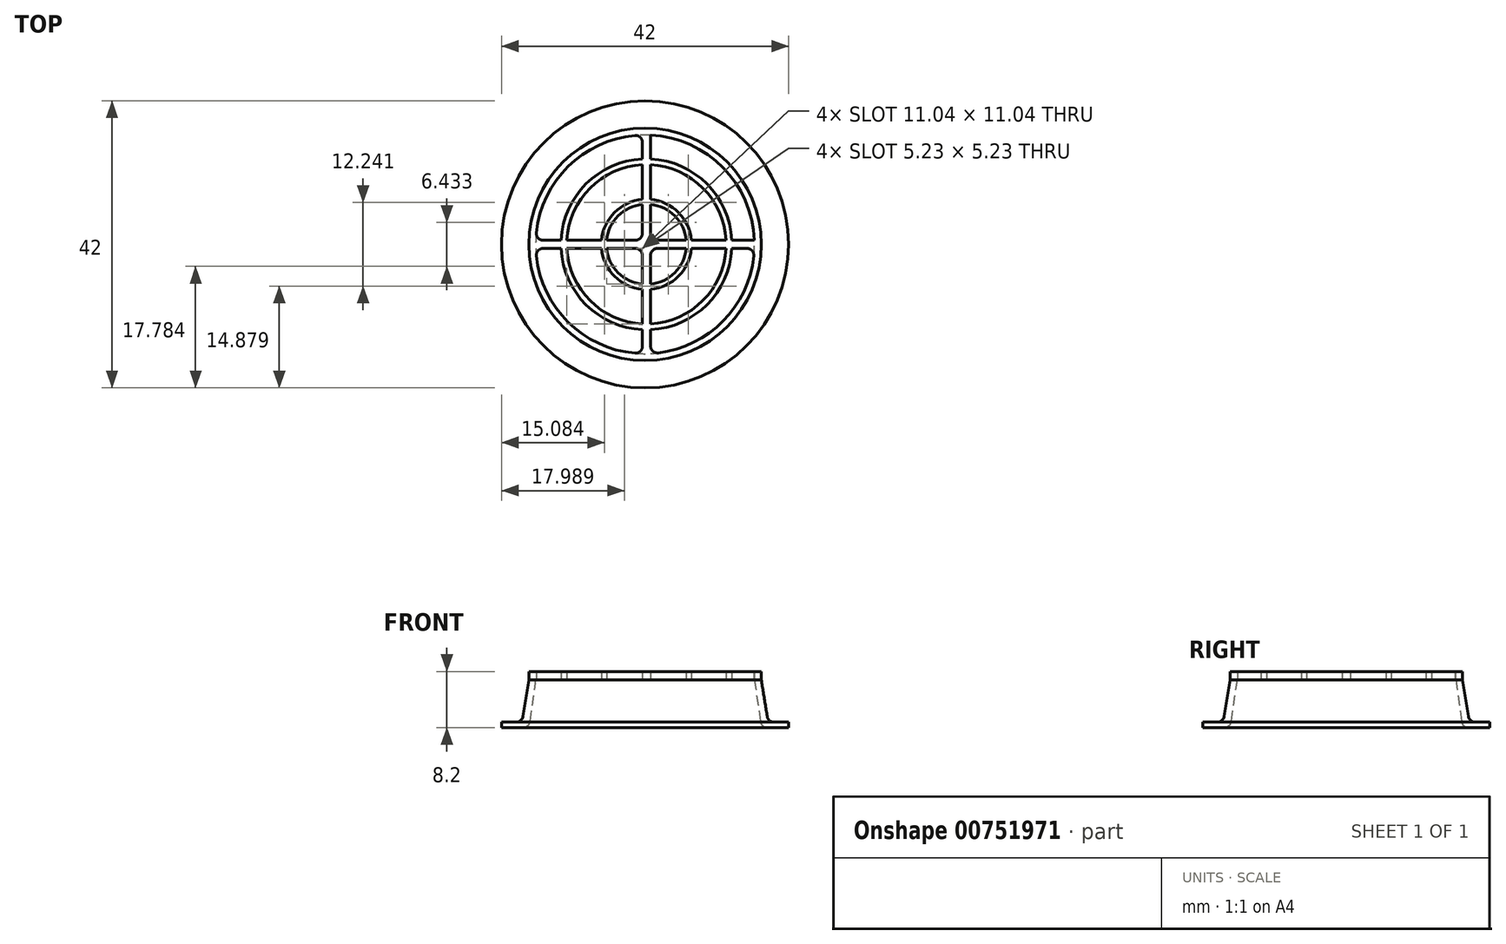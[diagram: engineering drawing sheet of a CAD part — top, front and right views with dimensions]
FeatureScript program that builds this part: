
annotation { "Feature Type Name" : "Feature", "Feature Type Description" : "" }
export const myFeature = defineFeature(function(context is Context, id is Id, definition is map)
    precondition{}
    {
        {
            var Q0;
            Q0=qCreatedBy(makeId("Front.planeOp"),FACE);
            var sketch = newSketch(context, id + "F0", { "sketchPlane" : qUnion([Q0])});
            skLineSegment(sketch, "E0", {"start": v(0, 16.66) * mm, "end": v(0, -15.75) * mm, "construction": true});
            skLineSegment(sketch, "E1", {"start": v(8.08, 0) * mm, "end": v(-29.3, 0) * mm, "construction": true});
            skLineSegment(sketch, "E2", {"start": v(1.58, 0) * mm, "end": v(-1.66, 0) * mm, "construction": true});
            skLineSegment(sketch, "E3", {"start": v(-1, 1.45) * mm, "end": v(-1, -7.95) * mm, "construction": true});
            skLineSegment(sketch, "E4", {"start": v(-5, -6.2) * mm, "end": v(-5, -8.06) * mm, "construction": true});
            skLineSegment(sketch, "E5", {"start": v(-5, -7) * mm, "end": v(-1.87, -7) * mm});
            skLineSegment(sketch, "E6", {"start": v(-0.88, -6.14) * mm, "end": v(0, 0) * mm});
            skLineSegment(sketch, "E7", {"start": v(0, 0) * mm, "end": v(-1, 0) * mm});
            skLineSegment(sketch, "E8", {"start": v(-1, 0) * mm, "end": v(-1.86, -5.36) * mm});
            skLineSegment(sketch, "E9", {"start": v(-2.85, -6.2) * mm, "end": v(-5, -6.2) * mm});
            skLineSegment(sketch, "E10", {"start": v(-5, -6.2) * mm, "end": v(-5, -7) * mm});
            skPoint(sketch, "E11.visualSharp", {"position": v(-2, -6.2) * mm});
            skArc(sketch, "E11.filletArc", {"start": v(-2.85, -6.2) * mm, "mid": v(-2.2, -5.96) * mm, "end": v(-1.86, -5.36) * mm});
            skPoint(sketch, "E12.visualSharp", {"position": v(-1, -7) * mm});
            skArc(sketch, "E12.filletArc", {"start": v(-1.87, -7) * mm, "mid": v(-1.21, -6.76) * mm, "end": v(-0.88, -6.14) * mm});
            skLineSegment(sketch, "E13", {"start": v(16, 0.36) * mm, "end": v(16, -7.36) * mm, "construction": true});
            skSolve(sketch);
        }
        {
            var Q0;
            Q0 = qSketchRegion(id + "F0", true);
            var Q1;
            Q1=sQuery(id+"F0.wireOp",EDGE,"E13");
            revolve(context, id + "F1", {"surfaceOperationType" : NewSurfaceOperationType.NEW, "entities" : qUnion([Q0]), "axis" : qUnion([Q1]), "revolveType" : RevolveType.FULL});
        }
        {
            var Q0;
            Q0=qCreatedBy(makeId("Top.planeOp"),FACE);
            var sketch = newSketch(context, id + "F2", { "sketchPlane" : qUnion([Q0])});
            skLineSegment(sketch, "E14", {"start": v(0, 0) * mm, "end": v(32.4, 0) * mm, "construction": true});
            skLineSegment(sketch, "E15", {"start": v(0.01, 0.6) * mm, "end": v(3.72, 0.6) * mm});
            skLineSegment(sketch, "E16.MirrorCS", {"start": v(0.01, -0.6) * mm, "end": v(3.72, -0.6) * mm});
            skLineSegment(sketch, "E17", {"start": v(16.2, 0) * mm, "end": v(16.2, 17) * mm, "construction": true});
            skLineSegment(sketch, "E18", {"start": v(15.6, 16) * mm, "end": v(15.6, 12.48) * mm});
            skLineSegment(sketch, "E19.MirrorCS", {"start": v(16.8, 15.98) * mm, "end": v(16.8, 12.48) * mm});
            skArc(sketch, "E20", {"start": v(15.6, 5.83) * mm, "mid": v(12.06, 4.15) * mm, "end": v(10.37, 0.6) * mm});
            skArc(sketch, "E21", {"start": v(15.6, 11.64) * mm, "mid": v(7.96, 8.24) * mm, "end": v(4.56, 0.6) * mm});
            skArc(sketch, "E22", {"start": v(15.6, 6.58) * mm, "mid": v(11.53, 4.67) * mm, "end": v(9.63, 0.6) * mm});
            skArc(sketch, "E23", {"start": v(15.6, 12.48) * mm, "mid": v(7.37, 8.84) * mm, "end": v(3.72, 0.6) * mm});
            skLineSegment(sketch, "E24.trimOffspring", {"start": v(16.8, 11.64) * mm, "end": v(16.8, 6.58) * mm});
            skLineSegment(sketch, "E25.trimOffspring", {"start": v(15.6, 11.64) * mm, "end": v(15.6, 6.58) * mm});
            skLineSegment(sketch, "E26.trimOffspring", {"start": v(15.6, 5.83) * mm, "end": v(15.6, 1.6) * mm});
            skLineSegment(sketch, "E27.trimOffspring", {"start": v(16.8, 5.83) * mm, "end": v(16.8, 1.6) * mm});
            skArc(sketch, "E28.trimOffspring", {"start": v(27.85, 0.6) * mm, "mid": v(24.45, 8.24) * mm, "end": v(16.8, 11.64) * mm});
            skLineSegment(sketch, "E29.trimOffspring", {"start": v(28.69, -0.6) * mm, "end": v(31.99, -0.6) * mm});
            skArc(sketch, "E30.trimOffspring", {"start": v(28.69, 0.6) * mm, "mid": v(25.04, 8.84) * mm, "end": v(16.8, 12.48) * mm});
            skLineSegment(sketch, "E31.trimOffspring", {"start": v(28.69, 0.6) * mm, "end": v(31.99, 0.6) * mm});
            skArc(sketch, "E32.trimOffspring", {"start": v(3.72, -0.6) * mm, "mid": v(7.37, -8.84) * mm, "end": v(15.6, -12.48) * mm});
            skArc(sketch, "E33.trimOffspring", {"start": v(4.56, -0.6) * mm, "mid": v(7.96, -8.24) * mm, "end": v(15.6, -11.64) * mm});
            skLineSegment(sketch, "E34.trimOffspring", {"start": v(4.56, 0.6) * mm, "end": v(9.63, 0.6) * mm});
            skLineSegment(sketch, "E35.trimOffspring", {"start": v(4.56, -0.6) * mm, "end": v(9.63, -0.6) * mm});
            skArc(sketch, "E36.trimOffspring", {"start": v(9.63, -0.6) * mm, "mid": v(11.53, -4.67) * mm, "end": v(15.6, -6.58) * mm});
            skLineSegment(sketch, "E37.trimOffspring", {"start": v(10.37, 0.6) * mm, "end": v(14.6, 0.6) * mm});
            skArc(sketch, "E38.trimOffspring", {"start": v(10.37, -0.6) * mm, "mid": v(12.06, -4.15) * mm, "end": v(15.6, -5.83) * mm});
            skLineSegment(sketch, "E39.trimOffspring", {"start": v(10.37, -0.6) * mm, "end": v(14.6, -0.6) * mm});
            skArc(sketch, "E40.trimOffspring", {"start": v(22.04, 0.6) * mm, "mid": v(20.35, 4.15) * mm, "end": v(16.8, 5.83) * mm});
            skLineSegment(sketch, "E41.trimOffspring", {"start": v(22.78, -0.6) * mm, "end": v(27.85, -0.6) * mm});
            skArc(sketch, "E42.trimOffspring", {"start": v(22.78, 0.6) * mm, "mid": v(20.88, 4.67) * mm, "end": v(16.8, 6.58) * mm});
            skLineSegment(sketch, "E43.trimOffspring", {"start": v(15.6, -6.58) * mm, "end": v(15.6, -11.64) * mm});
            skArc(sketch, "E44.trimOffspring", {"start": v(16.8, -6.58) * mm, "mid": v(20.88, -4.67) * mm, "end": v(22.78, -0.6) * mm});
            skLineSegment(sketch, "E45.trimOffspring", {"start": v(16.8, -6.58) * mm, "end": v(16.8, -11.64) * mm});
            skArc(sketch, "E46.trimOffspring", {"start": v(16.8, -5.83) * mm, "mid": v(20.35, -4.15) * mm, "end": v(22.04, -0.6) * mm});
            skLineSegment(sketch, "E47.trimOffspring", {"start": v(15.6, -12.48) * mm, "end": v(15.6, -16) * mm});
            skArc(sketch, "E48.trimOffspring", {"start": v(16.8, -12.48) * mm, "mid": v(25.04, -8.84) * mm, "end": v(28.69, -0.6) * mm});
            skLineSegment(sketch, "E49.trimOffspring", {"start": v(16.8, -12.48) * mm, "end": v(16.8, -16) * mm});
            skArc(sketch, "E50.trimOffspring", {"start": v(16.8, -11.64) * mm, "mid": v(24.45, -8.24) * mm, "end": v(27.85, -0.6) * mm});
            skLineSegment(sketch, "E51", {"start": v(17.8, 0.6) * mm, "end": v(22.04, 0.6) * mm});
            skLineSegment(sketch, "E52", {"start": v(16.8, -1.6) * mm, "end": v(16.8, -5.83) * mm});
            skLineSegment(sketch, "E53", {"start": v(17.8, -0.6) * mm, "end": v(22.04, -0.6) * mm});
            skLineSegment(sketch, "E54.trimOffspring", {"start": v(15.6, -1.6) * mm, "end": v(15.6, -5.83) * mm});
            skPoint(sketch, "E55.visualSharp", {"position": v(15.6, 0.6) * mm});
            skArc(sketch, "E55.filletArc", {"start": v(14.6, 0.6) * mm, "mid": v(15.31, 0.9) * mm, "end": v(15.6, 1.6) * mm});
            skPoint(sketch, "E56.visualSharp", {"position": v(16.8, 0.6) * mm});
            skArc(sketch, "E56.filletArc", {"start": v(16.8, 1.6) * mm, "mid": v(17.1, 0.9) * mm, "end": v(17.8, 0.6) * mm});
            skPoint(sketch, "E57.visualSharp", {"position": v(16.8, -0.6) * mm});
            skArc(sketch, "E57.filletArc", {"start": v(17.8, -0.6) * mm, "mid": v(17.1, -0.9) * mm, "end": v(16.8, -1.6) * mm});
            skPoint(sketch, "E58.visualSharp", {"position": v(15.6, -0.6) * mm});
            skArc(sketch, "E58.filletArc", {"start": v(15.6, -1.6) * mm, "mid": v(15.31, -0.9) * mm, "end": v(14.6, -0.6) * mm});
            skLineSegment(sketch, "E59.trimOffspring", {"start": v(22.78, 0.6) * mm, "end": v(27.85, 0.6) * mm});
            skCircle(sketch, "E60.0", {"center": v(16, 0) * mm, "radius": 16 * mm});
            skPoint(sketch, "E61.orphan", {"position": v(16.8, 16) * mm});
            skSolve(sketch);
        }
        {
            var Q0;
            Q0=makeQuery(id+"F1.opRevolve","SWEPT_FACE",FACE,{"disambiguationData":[OSD([sQuery(id+"F0.wireOp",EDGE,"E7")])]});
            var Q1;
            {var subQ7=sQuery(id+"F2.wireOp",EDGE,"E15");Q1=makeQuery(id+"F2.imprint","IMPRINT",FACE,{"disambiguationData":[TD([[makeQuery(id+"F2.imprint","IMPRINT",EDGE,{"derivedFrom":subQ7}),-1.0]])]});}
            extrude(context, id + "F3", {"entities" : qUnion([Q0, Q1]), "operationType" : NewBodyOperationType.ADD, "depth" : 1.2 * mm, "offsetDistance" : 25 * mm});
        }
        {
            var Q0;
            Q0=makeQuery(id+"F3.opExtrude","SWEPT_EDGE",EDGE,{"disambiguationData":[OSD([sQuery(id+"F2.wireOp",EDGE,"E18"),sQuery(id+"F2.wireOp",EDGE,"E60.0")])]});
            var Q1;
            Q1=makeQuery(id+"F3.opExtrude","SWEPT_EDGE",EDGE,{"disambiguationData":[OSD([sQuery(id+"F2.wireOp",EDGE,"E19.MirrorCS"),sQuery(id+"F2.wireOp",EDGE,"E60.0")])]});
            var Q2;
            Q2=makeQuery(id+"F3.opExtrude","SWEPT_EDGE",EDGE,{"disambiguationData":[OSD([sQuery(id+"F2.wireOp",EDGE,"E29.trimOffspring"),sQuery(id+"F2.wireOp",EDGE,"E60.0")])]});
            var Q3;
            Q3=makeQuery(id+"F3.opExtrude","SWEPT_EDGE",EDGE,{"disambiguationData":[OSD([sQuery(id+"F2.wireOp",EDGE,"E31.trimOffspring"),sQuery(id+"F2.wireOp",EDGE,"E60.0")])]});
            var Q4;
            Q4=makeQuery(id+"F3.opExtrude","SWEPT_EDGE",EDGE,{"disambiguationData":[OSD([sQuery(id+"F2.wireOp",EDGE,"E47.trimOffspring"),sQuery(id+"F2.wireOp",EDGE,"E60.0")])]});
            var Q5;
            Q5=makeQuery(id+"F3.opExtrude","SWEPT_EDGE",EDGE,{"disambiguationData":[OSD([sQuery(id+"F2.wireOp",EDGE,"E49.trimOffspring"),sQuery(id+"F2.wireOp",EDGE,"E60.0")])]});
            var Q6;
            Q6=makeQuery(id+"F3.opExtrude","SWEPT_EDGE",EDGE,{"disambiguationData":[OSD([sQuery(id+"F2.wireOp",EDGE,"E15"),sQuery(id+"F2.wireOp",EDGE,"E60.0")])]});
            var Q7;
            Q7=makeQuery(id+"F3.opExtrude","SWEPT_EDGE",EDGE,{"disambiguationData":[OSD([sQuery(id+"F2.wireOp",EDGE,"E16.MirrorCS"),sQuery(id+"F2.wireOp",EDGE,"E60.0")])]});
            fillet(context, id + "F4", {"entities" : qUnion([Q0, Q1, Q2, Q3, Q4, Q5, Q6, Q7]), "radius" : 1 * mm, "tangentPropagation" : true, "allowEdgeOverflow" : false});
        }
    });
